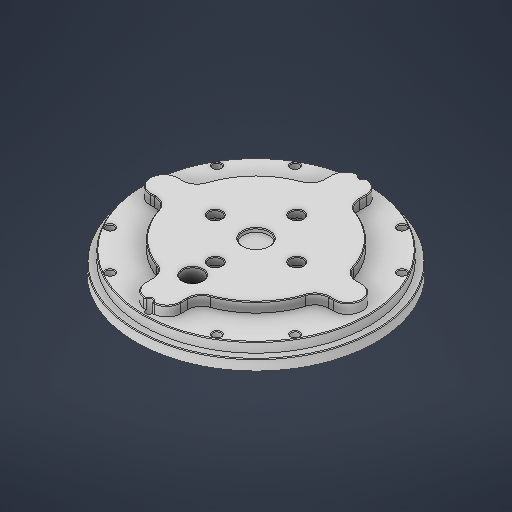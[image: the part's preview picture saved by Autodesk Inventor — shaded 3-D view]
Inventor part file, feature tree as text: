
AUTODESK INVENTOR PART (.ipt)
format: ipt  version: 2025 (Build 290162000, 162)  size: 609,792 bytes
history: native  units: in
note: dims shown in document units (in); Inventor stores cm internally (conversion verified against a paired STEP export)
features: sketch x17, extrude x11, hole x4, chamfer x4
ambient origin geometry x8: Origin, YZ Plane, XZ Plane, XY Plane, X Axis, Y Axis, Z Axis, Center Point
bodies: Solid1 (feature_tree)
feature tree (36):
  sketch  "Sketch1"  dims[d3=4.3307in d24=6.6929in]
  extrude  "Extrusion1"  Depth=6.6929in
  extrude  "Extrusion2"  Depth=5.9843in
  extrude  "Extrusion3"  Depth=0.9843in
  sketch  "Sketch2"  dims[d27=0.9843in d28=4.3307in]
  extrude  "Extrusion4"  Depth=0.3937in
  hole  "Hole1"  [1 undecoded]
  hole  "Hole2"  [1 undecoded]
  sketch  "Sketch4"  dims[d38=0.2953in d39=0.0in d40=2.2835in]
  extrude  "Extrusion5"  Depth=2.2835in
  extrude  "Extrusion6"  Depth=0.3543in
  hole  "Hole3"  [1 undecoded]
  chamfer  "Chamfer1"  Distance=0.7874in Angle=360.0deg
  chamfer  "Chamfer2"  Distance=0.0591in
  hole  "Hole5"  [1 undecoded]
  extrude  "Extrusion9"  Depth=0.1673in TaperAngle=360.0deg
  chamfer  "Chamfer3"  Distance=0.0197in Angle=45.0deg
  extrude  "Extrusion10"  Depth=0.1673in TaperAngle=45.0deg
  chamfer  "Chamfer4"  Distance=3.7402in
  sketch  "Sketch11"  dims[d74=0.4724in d75=0.0in d76=0.1969in d77=4.7244in d79=360.0deg d81=0.2165in d82=0.3937in d83=0.1575in d84=0.0787in d85=90.0deg d86=0.3937in d87=0.8108in d88=0.0197in d89=0.0787in d90=45.0deg d91=0.0197in d92=0.0787in d93=45.0deg d107=3.7402in d108=0.1969in d109=6.2992in d111=360.0deg d113=0.1969in d114=0.7874in d115=0.748in d116=0.3543in d117=90.0deg d118=0.7874in d119=0.8108in d139=0.7185in d140=3.1496in d141=0.7185in d142=3.1496in d144=360.0deg d146=0.0984in d147=0.0in d148=0.0197in d149=0.0787in d150=45.0deg d151=0.5512in d152=1.7717in d153=0.0in d154=0.0in d155=0.0197in d156=0.0787in d157=45.0deg d158=0.5512in d159=1.7717in d160=0.3159in d161=4.7244in d163=360.0deg d165=0.2756in d166=0.7874in d168=360.0deg d170=0.3159in d171=1.5748in d173=360.0deg d175=0.1673in d176=0.0in d177=0.1575in d178=0.0in d179=0.1673in d180=0.0in d137=0.0197in d138=0.0344in]
  extrude  "Extrusion11"  Depth=0.1673in
  extrude  "Extrusion12"  Depth=0.1673in TaperAngle=360.0deg
  extrude  "Extrusion13"  Depth=0.1673in
  sketch  "Sketch Circular Pattern1"  dims[d25=6.2992in d26=5.9843in]
  sketch  "Sketch3"  dims[d31=0.3937in d32=0.3937in]
  sketch  "Sketch Circular Pattern2"  dims[d29=0.7874in d30=0.3937in]
  sketch  "Sketch5"  dims[d41=0.3543in d42=0.1969in]
  sketch  "Sketch Circular Pattern3"  dims[d34=0.8465in d35=0.0in d36=0.5709in d37=0.0in]
  sketch  "Sketch7"  dims[d56=5.9843in]
  sketch  "Sketch Circular Pattern5"  dims[d43=1.5748in d45=360.0deg d47=0.1969in d48=0.0in]
  sketch  "Sketch9"  dims[d69=3.1496in]
  sketch  "Sketch Circular Pattern6"  dims[d49=0.2165in d50=0.7874in d51=0.1575in d52=0.0787in d53=90.0deg d54=0.315in d55=0.8108in]
  sketch  "Sketch10"  dims[d71=0.7874in d72=0.0591in d73=0.0in]
  sketch  "Sketch Circular Pattern7"  dims[d57=0.1378in d58=0.7874in d60=360.0deg]
  sketch  "Sketch Circular Pattern8"  dims[d62=0.1772in d63=0.315in d64=0.1575in d65=0.0787in d66=90.0deg d67=0.4646in d68=0.8108in]
  sketch  "Sketch Circular Pattern9"  dims[d70=0.1969in]
note: 4 required parameter values undecoded (feature->parameter linkage not recoverable at this tier; creation-order binding heuristic only, values carry confidence <= 0.55)
